# Revit family: Faucet-Kitchen-American_Standard-Avery-4901.410
name_source: partatom
category: Plumbing Fixtures
revit_build: Autodesk Revit 2014 (Build: 20130308_1515(x64)
units: mm (PartAtom-declared; Revit-internal decimal feet)

## types (1)
- 4901.410
    ADA Compliant = Yes
    Assembly Code = D2020300
    CW Connection = Yes
    CWFU = 1.5
    Cold Water Connection Diameter = 3/8"
    Cold Water Connection Radius = 3/16"
    Default Elevation = 0"
    Description = American Standard Avery Pull-Down Bar Faucet
    Escutcheon plate = No
    Flow Rate = 1.5 gpm (5.7 L/min)
    HW Connection = Yes
    HWFU = 1.5
    Height = 15"
    Hot Water Connection Diameter = 0"
    Hot Water Connection Radius = 3/16"
    Installation Type = Mounted
    Length = 6 1/2"
    Manufacturer = American Standard
    Material = Metal-American Standard-002-Polished Chrome
    Model = 4901.410
    Price = Prices may vary. Please consult Manufacturer Representative for most up-to-date price list.
    Product Documentation Link = https://www.americanstandard-us.com
    Product Page URL = https://www.americanstandard-us.com
    URL = https://www.americanstandard-us.com
    Vent Connection = No
    WFU = 2
    Warranty Information = Limited Lifetime Function and Finish Warranty. 5 Years Commercial.
    Waste Connection = Yes
    Width = 6 1/4"

## geometry (parser evidence)
native form markers: Sweep x1
no freeform markers — native parametric forms only
